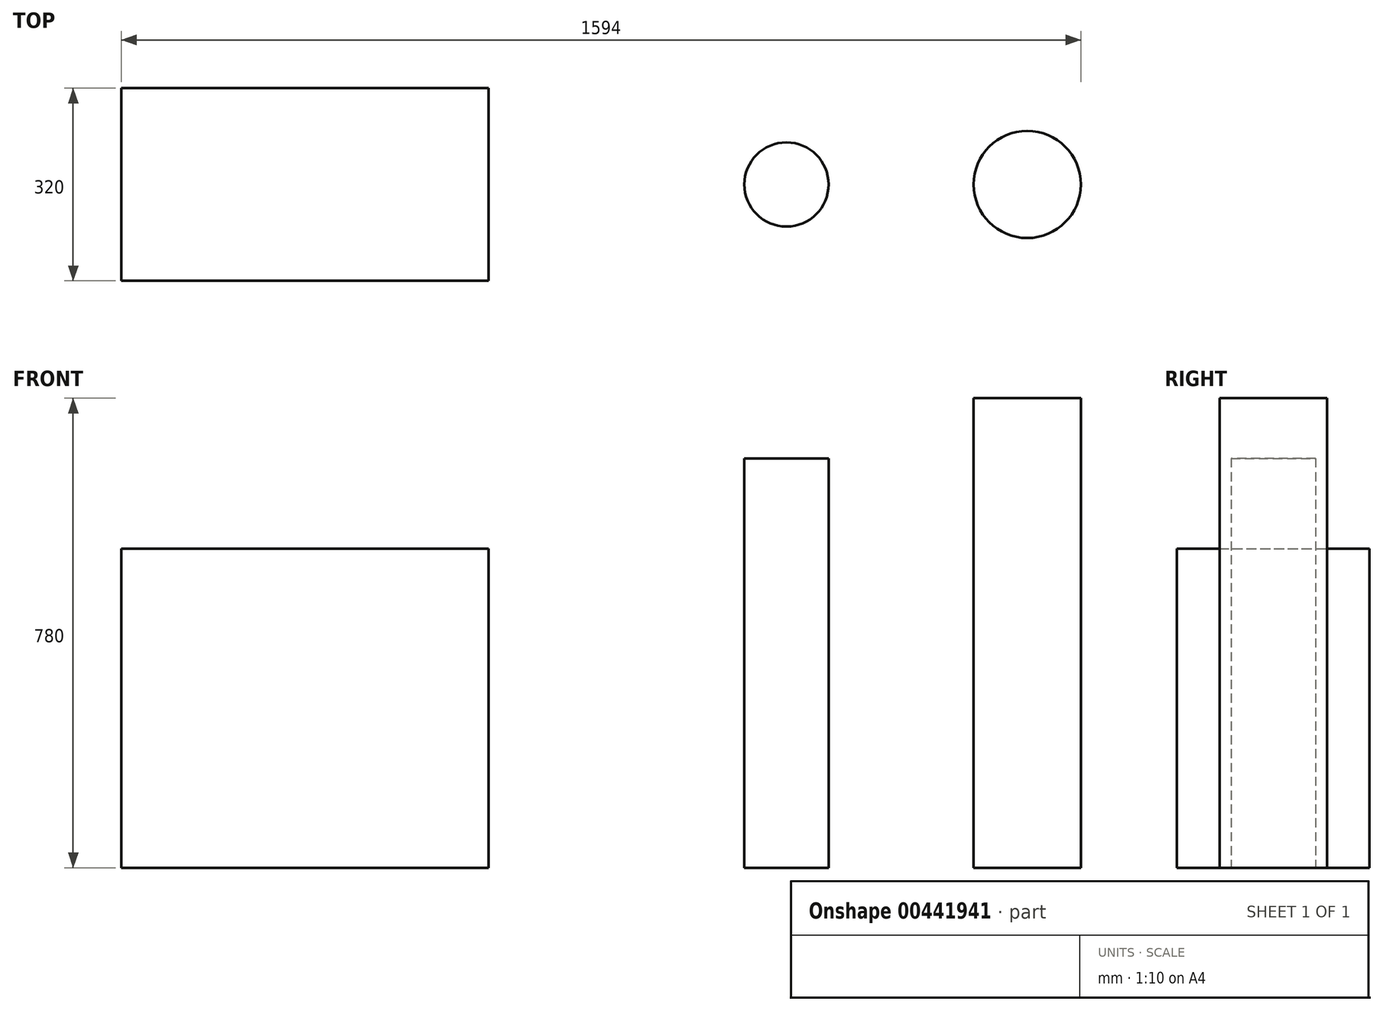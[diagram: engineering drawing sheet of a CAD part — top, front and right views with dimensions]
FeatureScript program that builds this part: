
annotation { "Feature Type Name" : "Feature", "Feature Type Description" : "" }
export const myFeature = defineFeature(function(context is Context, id is Id, definition is map)
    precondition{}
    {
        {
            var Q0;
            Q0=qCreatedBy(makeId("Top.planeOp"),FACE);
            var sketch = newSketch(context, id + "F0", { "sketchPlane" : qUnion([Q0])});
            skLineSegment(sketch, "E0.bottom", {"start": v(305, -160) * mm, "end": v(-305, -160) * mm});
            skLineSegment(sketch, "E0.top", {"start": v(305, 160) * mm, "end": v(-305, 160) * mm});
            skLineSegment(sketch, "E0.left", {"start": v(305, -160) * mm, "end": v(305, 160) * mm});
            skLineSegment(sketch, "E0.right", {"start": v(-305, -160) * mm, "end": v(-305, 160) * mm});
            skPoint(sketch, "E0.middle", {"position": v(0, 0) * mm});
            skSolve(sketch);
        }
        {
            var Q0;
            Q0 = qSketchRegion(id + "F0", true);
            extrude(context, id + "F1", {"entities" : qUnion([Q0]), "depth" : 530 * mm});
        }
        {
            var Q0;
            Q0=qCreatedBy(makeId("Top.planeOp"),FACE);
            var sketch = newSketch(context, id + "F2", { "sketchPlane" : qUnion([Q0])});
            skCircle(sketch, "E1", {"center": v(800, 0) * mm, "radius": 70 * mm});
            skCircle(sketch, "E2", {"center": v(1200, 0) * mm, "radius": 89 * mm});
            skSolve(sketch);
        }
        {
            var Q0;
            Q0=makeQuery(id+"F2.imprint","IMPRINT",FACE,{"disambiguationData":[TD([[makeQuery(id+"F2.imprint","IMPRINT",EDGE,{"derivedFrom":sQuery(id+"F2.wireOp",EDGE,"E1")}),1.0]])]});
            extrude(context, id + "F3", {"entities" : qUnion([Q0]), "depth" : 680 * mm});
        }
        {
            var Q0;
            Q0=makeQuery(id+"F2.imprint","IMPRINT",FACE,{"disambiguationData":[TD([[makeQuery(id+"F2.imprint","IMPRINT",EDGE,{"derivedFrom":sQuery(id+"F2.wireOp",EDGE,"E2")}),1.0]])]});
            extrude(context, id + "F4", {"entities" : qUnion([Q0]), "depth" : 780 * mm});
        }
    });
